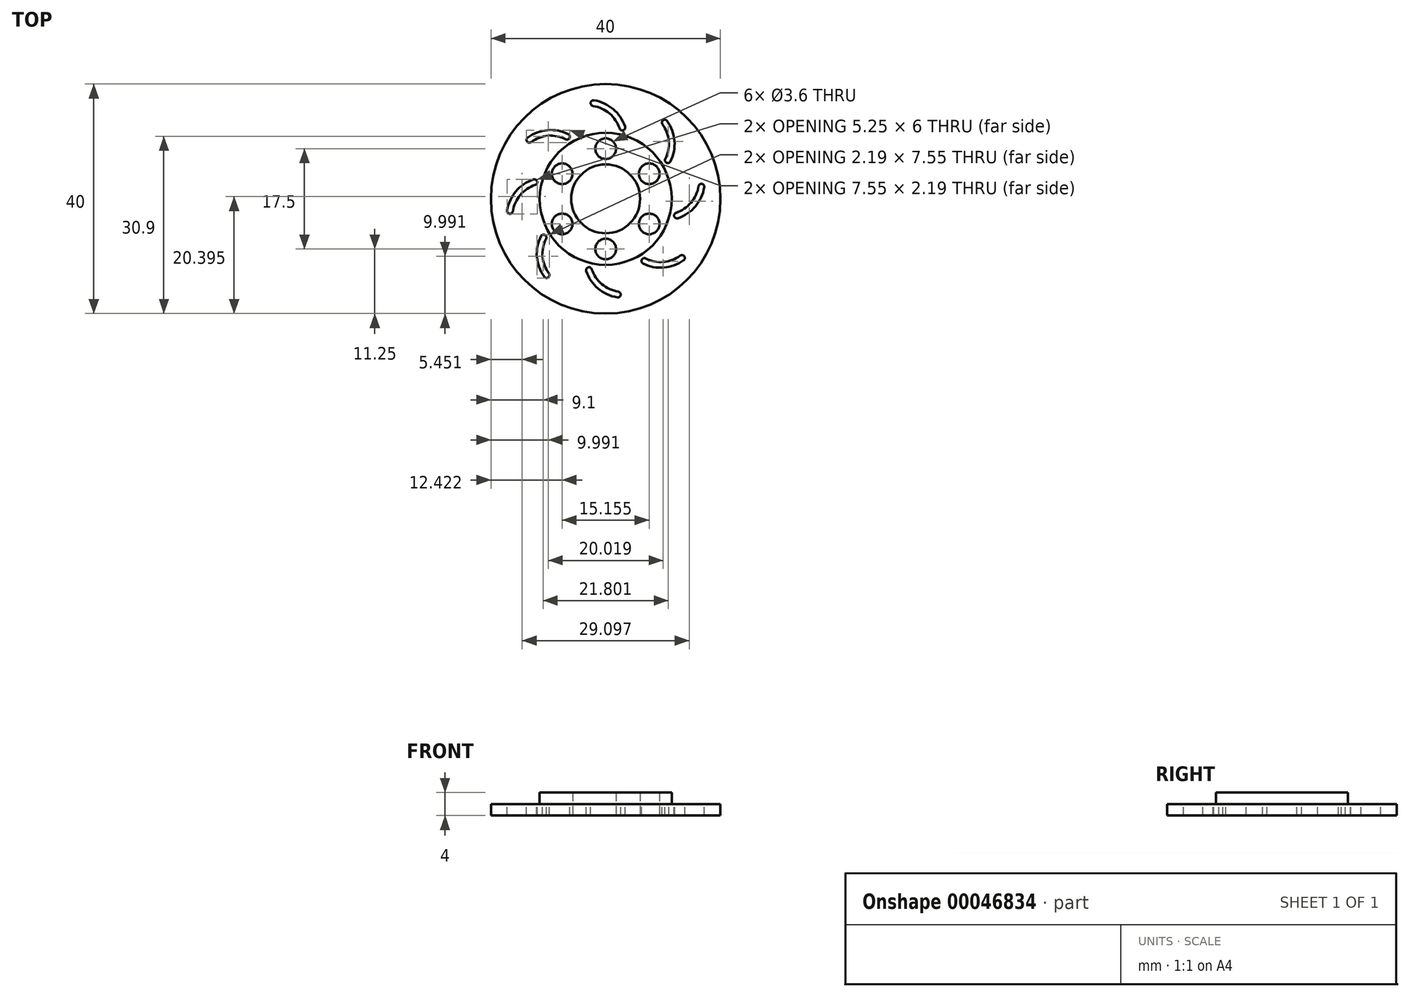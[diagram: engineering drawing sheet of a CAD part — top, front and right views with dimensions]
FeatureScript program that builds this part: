
annotation { "Feature Type Name" : "Feature", "Feature Type Description" : "" }
export const myFeature = defineFeature(function(context is Context, id is Id, definition is map)
    precondition{}
    {
        {
            var Q0;
            Q0=qCreatedBy(makeId("Top.planeOp"),FACE);
            var sketch = newSketch(context, id + "F0", { "sketchPlane" : qUnion([Q0])});
            skCircle(sketch, "E0", {"center": v(0, 0) * mm, "radius": 6 * mm});
            skCircle(sketch, "E1", {"center": v(0, 0) * mm, "radius": 11.5 * mm});
            skCircle(sketch, "E2", {"center": v(0, 0) * mm, "radius": 20 * mm});
            skCircle(sketch, "E3", {"center": v(0, 8.75) * mm, "radius": 1.8 * mm});
            skCircle(sketch, "E4.1.0", {"center": v(-7.58, 4.38) * mm, "radius": 1.8 * mm});
            skCircle(sketch, "E4.2.0", {"center": v(-7.58, -4.37) * mm, "radius": 1.8 * mm});
            skCircle(sketch, "E4.3.0", {"center": v(0, -8.75) * mm, "radius": 1.8 * mm});
            skCircle(sketch, "E4.4.0", {"center": v(7.58, -4.38) * mm, "radius": 1.8 * mm});
            skCircle(sketch, "E4.5.0", {"center": v(7.58, 4.38) * mm, "radius": 1.8 * mm});
            skSolve(sketch);
        }
        {
            var Q0;
            Q0=makeQuery(id+"F0.imprint","IMPRINT",FACE,{"disambiguationData":[TD([[makeQuery(id+"F0.imprint","IMPRINT",EDGE,{"derivedFrom":sQuery(id+"F0.wireOp",EDGE,"E0")}),-1.0]])]});
            extrude(context, id + "F1", {"entities" : qUnion([Q0]), "depth" : 4 * mm});
        }
        {
            var Q0;
            Q0=makeQuery(id+"F0.imprint","IMPRINT",FACE,{"disambiguationData":[TD([[makeQuery(id+"F0.imprint","IMPRINT",EDGE,{"derivedFrom":sQuery(id+"F0.wireOp",EDGE,"E1")}),-1.0]])]});
            extrude(context, id + "F2", {"entities" : qUnion([Q0]), "operationType" : NewBodyOperationType.ADD, "depth" : 2 * mm});
        }
        {
            var Q0;
            Q0=makeQuery(id+"F2.opExtrude","CAP_FACE",FACE,{"disambiguationData":[OSD([sQuery(id+"F0.wireOp",EDGE,"E1"),sQuery(id+"F0.wireOp",EDGE,"E2")])],"isStart":false});
            var sketch = newSketch(context, id + "F3", { "sketchPlane" : qUnion([Q0])});
            skArc(sketch, "E5", {"start": v(2.42, 12.26) * mm, "mid": v(0.66, 14.87) * mm, "end": v(-2.2, 16.19) * mm});
            skArc(sketch, "E6.0", {"start": v(3.37, 12.58) * mm, "mid": v(1.31, 15.63) * mm, "end": v(-2.03, 17.18) * mm});
            skArc(sketch, "E7", {"start": v(-2.03, 17.18) * mm, "mid": v(-2.6, 16.76) * mm, "end": v(-2.2, 16.19) * mm});
            skArc(sketch, "E8", {"start": v(2.42, 12.26) * mm, "mid": v(3.06, 11.95) * mm, "end": v(3.37, 12.58) * mm});
            skArc(sketch, "E9.1.0", {"start": v(-6.5, 11.28) * mm, "mid": v(-10.13, 11.98) * mm, "end": v(-13.58, 10.7) * mm});
            skArc(sketch, "E9.1.1", {"start": v(-6.96, 10.39) * mm, "mid": v(-10.05, 10.99) * mm, "end": v(-13, 9.9) * mm});
            skArc(sketch, "E9.1.2", {"start": v(-6.96, 10.39) * mm, "mid": v(-6.29, 10.6) * mm, "end": v(-6.5, 11.28) * mm});
            skArc(sketch, "E9.1.3", {"start": v(-13.58, 10.7) * mm, "mid": v(-13.7, 10) * mm, "end": v(-13, 9.9) * mm});
            skArc(sketch, "E9.2.0", {"start": v(-12.58, 3.37) * mm, "mid": v(-15.63, 1.31) * mm, "end": v(-17.18, -2.03) * mm});
            skArc(sketch, "E9.2.1", {"start": v(-12.26, 2.42) * mm, "mid": v(-14.87, 0.66) * mm, "end": v(-16.19, -2.2) * mm});
            skArc(sketch, "E9.2.2", {"start": v(-12.26, 2.42) * mm, "mid": v(-11.95, 3.06) * mm, "end": v(-12.58, 3.37) * mm});
            skArc(sketch, "E9.2.3", {"start": v(-17.18, -2.03) * mm, "mid": v(-16.76, -2.6) * mm, "end": v(-16.19, -2.2) * mm});
            skArc(sketch, "E9.3.0", {"start": v(-11.28, -6.5) * mm, "mid": v(-11.98, -10.13) * mm, "end": v(-10.7, -13.58) * mm});
            skArc(sketch, "E9.3.1", {"start": v(-10.39, -6.96) * mm, "mid": v(-10.99, -10.05) * mm, "end": v(-9.9, -13) * mm});
            skArc(sketch, "E9.3.2", {"start": v(-10.39, -6.96) * mm, "mid": v(-10.6, -6.29) * mm, "end": v(-11.28, -6.5) * mm});
            skArc(sketch, "E9.3.3", {"start": v(-10.7, -13.58) * mm, "mid": v(-10, -13.7) * mm, "end": v(-9.9, -13) * mm});
            skArc(sketch, "E9.4.0", {"start": v(-3.37, -12.58) * mm, "mid": v(-1.31, -15.63) * mm, "end": v(2.03, -17.18) * mm});
            skArc(sketch, "E9.4.1", {"start": v(-2.42, -12.26) * mm, "mid": v(-0.66, -14.87) * mm, "end": v(2.2, -16.19) * mm});
            skArc(sketch, "E9.4.2", {"start": v(-2.42, -12.26) * mm, "mid": v(-3.06, -11.95) * mm, "end": v(-3.37, -12.58) * mm});
            skArc(sketch, "E9.4.3", {"start": v(2.03, -17.18) * mm, "mid": v(2.6, -16.76) * mm, "end": v(2.2, -16.19) * mm});
            skArc(sketch, "E9.5.0", {"start": v(6.5, -11.28) * mm, "mid": v(10.13, -11.98) * mm, "end": v(13.58, -10.7) * mm});
            skArc(sketch, "E9.5.1", {"start": v(6.96, -10.39) * mm, "mid": v(10.05, -10.99) * mm, "end": v(13, -9.9) * mm});
            skArc(sketch, "E9.5.2", {"start": v(6.96, -10.39) * mm, "mid": v(6.29, -10.6) * mm, "end": v(6.5, -11.28) * mm});
            skArc(sketch, "E9.5.3", {"start": v(13.58, -10.7) * mm, "mid": v(13.7, -10) * mm, "end": v(13, -9.9) * mm});
            skPoint(sketch, "E9.center", {"position": v(0, 0) * mm});
            skArc(sketch, "E10.1.6.0", {"start": v(12.58, -3.37) * mm, "mid": v(15.63, -1.31) * mm, "end": v(17.18, 2.03) * mm});
            skArc(sketch, "E10.4.6.0", {"start": v(12.26, -2.42) * mm, "mid": v(14.87, -0.66) * mm, "end": v(16.19, 2.2) * mm});
            skArc(sketch, "E10.8.6.0", {"start": v(12.26, -2.42) * mm, "mid": v(11.95, -3.06) * mm, "end": v(12.58, -3.37) * mm});
            skArc(sketch, "E10.12.6.0", {"start": v(17.18, 2.03) * mm, "mid": v(16.76, 2.6) * mm, "end": v(16.19, 2.2) * mm});
            skArc(sketch, "E10.1.7.0", {"start": v(11.28, 6.5) * mm, "mid": v(11.98, 10.13) * mm, "end": v(10.7, 13.58) * mm});
            skArc(sketch, "E10.4.7.0", {"start": v(10.39, 6.96) * mm, "mid": v(10.99, 10.05) * mm, "end": v(9.9, 13) * mm});
            skArc(sketch, "E10.8.7.0", {"start": v(10.39, 6.96) * mm, "mid": v(10.6, 6.29) * mm, "end": v(11.28, 6.5) * mm});
            skArc(sketch, "E10.12.7.0", {"start": v(10.7, 13.58) * mm, "mid": v(10, 13.7) * mm, "end": v(9.9, 13) * mm});
            skSolve(sketch);
        }
        {
            var Q0;
            Q0=makeQuery(id+"F3.imprint","IMPRINT",FACE,{"disambiguationData":[TD([[makeQuery(id+"F3.imprint","IMPRINT",EDGE,{"derivedFrom":sQuery(id+"F3.wireOp",EDGE,"E5")}),-1.0]])]});
            var Q1;
            Q1=makeQuery(id+"F3.imprint","IMPRINT",FACE,{"disambiguationData":[TD([[makeQuery(id+"F3.imprint","IMPRINT",EDGE,{"derivedFrom":sQuery(id+"F3.wireOp",EDGE,"E9.5.0")}),1.0]])]});
            var Q2;
            Q2=makeQuery(id+"F3.imprint","IMPRINT",FACE,{"disambiguationData":[TD([[makeQuery(id+"F3.imprint","IMPRINT",EDGE,{"derivedFrom":sQuery(id+"F3.wireOp",EDGE,"E9.4.0")}),1.0]])]});
            var Q3;
            Q3=makeQuery(id+"F3.imprint","IMPRINT",FACE,{"disambiguationData":[TD([[makeQuery(id+"F3.imprint","IMPRINT",EDGE,{"derivedFrom":sQuery(id+"F3.wireOp",EDGE,"E9.3.0")}),1.0]])]});
            var Q4;
            Q4=makeQuery(id+"F3.imprint","IMPRINT",FACE,{"disambiguationData":[TD([[makeQuery(id+"F3.imprint","IMPRINT",EDGE,{"derivedFrom":sQuery(id+"F3.wireOp",EDGE,"E9.2.0")}),1.0]])]});
            var Q5;
            Q5=makeQuery(id+"F3.imprint","IMPRINT",FACE,{"disambiguationData":[TD([[makeQuery(id+"F3.imprint","IMPRINT",EDGE,{"derivedFrom":sQuery(id+"F3.wireOp",EDGE,"E9.1.0")}),1.0]])]});
            var Q6;
            Q6=makeQuery(id+"F3.imprint","IMPRINT",FACE,{"disambiguationData":[TD([[makeQuery(id+"F3.imprint","IMPRINT",EDGE,{"derivedFrom":sQuery(id+"F3.wireOp",EDGE,"E10.1.7.0")}),1.0]])]});
            var Q7;
            Q7=makeQuery(id+"F3.imprint","IMPRINT",FACE,{"disambiguationData":[TD([[makeQuery(id+"F3.imprint","IMPRINT",EDGE,{"derivedFrom":sQuery(id+"F3.wireOp",EDGE,"E10.1.6.0")}),1.0]])]});
            extrude(context, id + "F4", {"entities" : qUnion([Q0, Q1, Q2, Q3, Q4, Q5, Q6, Q7]), "operationType" : NewBodyOperationType.REMOVE, "endBound" : BoundingType.THROUGH_ALL, "oppositeDirection" : true, "depth" : 25 * mm});
        }
    });
